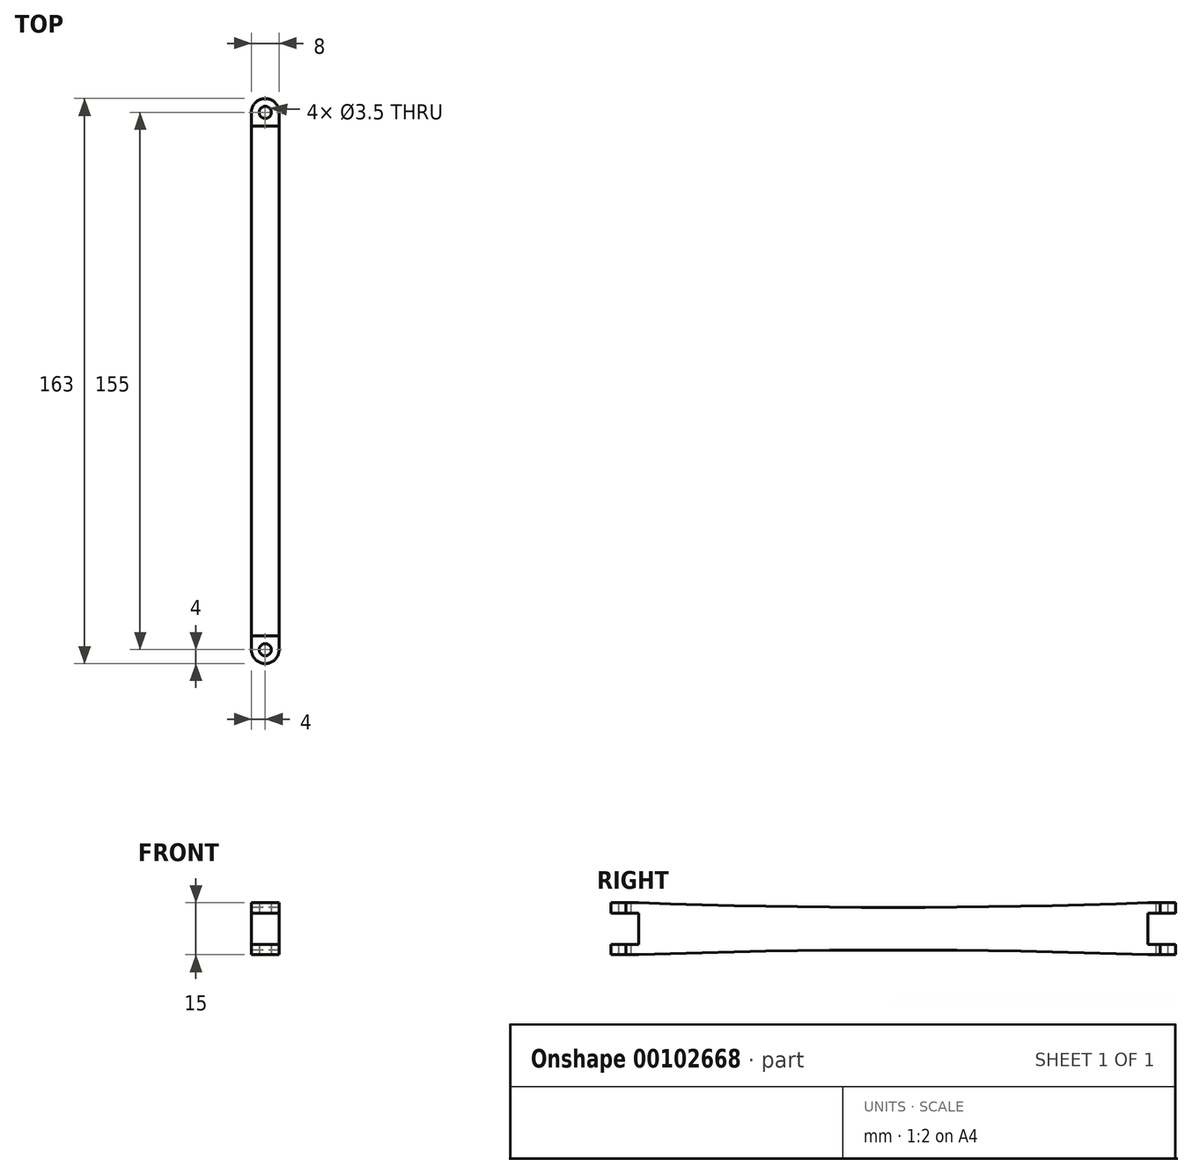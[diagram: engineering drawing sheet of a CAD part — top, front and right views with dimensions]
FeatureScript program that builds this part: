
annotation { "Feature Type Name" : "Feature", "Feature Type Description" : "" }
export const myFeature = defineFeature(function(context is Context, id is Id, definition is map)
    precondition{}
    {
        {
            var Q0;
            Q0=qCreatedBy(makeId("Top.planeOp"),FACE);
            var sketch = newSketch(context, id + "F0", { "sketchPlane" : qUnion([Q0])});
            skLineSegment(sketch, "E0", {"start": v(0, 0) * mm, "end": v(0, 155) * mm, "construction": true});
            skCircle(sketch, "E1", {"center": v(0, 155) * mm, "radius": 1.75 * mm});
            skCircle(sketch, "E2", {"center": v(0, 0) * mm, "radius": 1.75 * mm});
            skArc(sketch, "E3", {"start": v(3.98, 154.6) * mm, "mid": v(0, 159) * mm, "end": v(-3.98, 154.6) * mm});
            skArc(sketch, "E4", {"start": v(-3.98, 0.4) * mm, "mid": v(0, -4) * mm, "end": v(3.98, 0.4) * mm});
            skLineSegment(sketch, "E5", {"start": v(3.98, 0.4) * mm, "end": v(3.98, 154.6) * mm});
            skLineSegment(sketch, "E6", {"start": v(-3.98, 0.4) * mm, "end": v(-3.98, 154.6) * mm});
            skSolve(sketch);
        }
        {
            var Q0;
            Q0=makeQuery(id+"F0.imprint","IMPRINT",FACE,{"disambiguationData":[TD([[makeQuery(id+"F0.imprint","IMPRINT",EDGE,{"derivedFrom":sQuery(id+"F0.wireOp",EDGE,"E1")}),-1.0]])]});
            extrude(context, id + "F1", {"entities" : qUnion([Q0]), "depth" : 25 * mm});
        }
        {
            var Q0;
            Q0=qCreatedBy(makeId("Right.planeOp"),FACE);
            var sketch = newSketch(context, id + "F2", { "sketchPlane" : qUnion([Q0])});
            skLineSegment(sketch, "E7", {"start": v(0, 0) * mm, "end": v(-4, 0) * mm});
            skLineSegment(sketch, "E8", {"start": v(-4, 0) * mm, "end": v(-4, 3) * mm});
            skLineSegment(sketch, "E9", {"start": v(159, 3) * mm, "end": v(159, 0) * mm});
            skLineSegment(sketch, "E10", {"start": v(-4, 3) * mm, "end": v(4, 3) * mm});
            skLineSegment(sketch, "E11", {"start": v(4, 3) * mm, "end": v(4, 12) * mm});
            skLineSegment(sketch, "E12", {"start": v(4, 12) * mm, "end": v(-4, 12) * mm});
            skLineSegment(sketch, "E13", {"start": v(-4, 12) * mm, "end": v(-4, 15) * mm});
            skLineSegment(sketch, "E14", {"start": v(-4, 15) * mm, "end": v(4, 15) * mm});
            skArc(sketch, "E15", {"start": v(4, 15) * mm, "mid": v(77.5, 13.65) * mm, "end": v(151, 15) * mm});
            skLineSegment(sketch, "E16", {"start": v(151, 15) * mm, "end": v(159, 15) * mm});
            skLineSegment(sketch, "E17", {"start": v(159, 15) * mm, "end": v(159, 12) * mm});
            skLineSegment(sketch, "E18", {"start": v(159, 12) * mm, "end": v(151, 12) * mm});
            skLineSegment(sketch, "E19", {"start": v(151, 12) * mm, "end": v(151, 3) * mm});
            skLineSegment(sketch, "E20", {"start": v(151, 3) * mm, "end": v(159, 3) * mm});
            skLineSegment(sketch, "E21", {"start": v(0, 0) * mm, "end": v(4, 0) * mm});
            skLineSegment(sketch, "E22", {"start": v(159, 0) * mm, "end": v(151, 0) * mm});
            skArc(sketch, "E23", {"start": v(151, 0) * mm, "mid": v(77.5, 1.35) * mm, "end": v(4, 0) * mm});
            skSolve(sketch);
        }
        {
            var Q0;
            Q0=makeQuery(id+"F2.imprint","IMPRINT",FACE,{"disambiguationData":[TD([[makeQuery(id+"F2.imprint","IMPRINT",EDGE,{"derivedFrom":sQuery(id+"F2.wireOp",EDGE,"E7")}),-1.0]])]});
            extrude(context, id + "F3", {"entities" : qUnion([Q0]), "operationType" : NewBodyOperationType.INTERSECT, "endBound" : BoundingType.SYMMETRIC, "depth" : 25 * mm});
        }
    });
